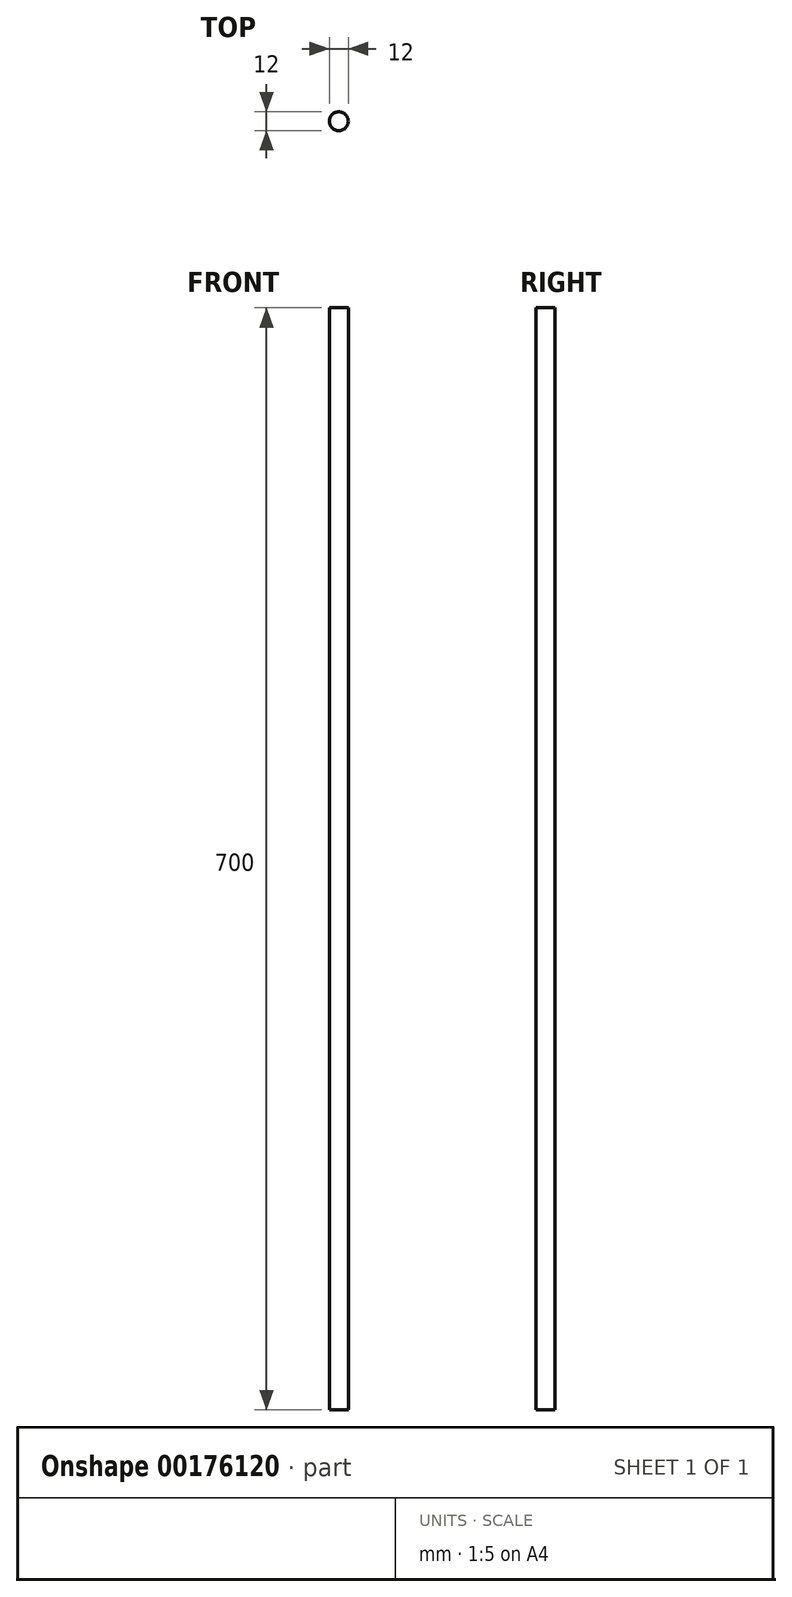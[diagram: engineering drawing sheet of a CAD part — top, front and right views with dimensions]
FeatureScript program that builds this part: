
annotation { "Feature Type Name" : "Feature", "Feature Type Description" : "" }
export const myFeature = defineFeature(function(context is Context, id is Id, definition is map)
    precondition{}
    {
        {
            var Q0;
            Q0=qCreatedBy(makeId("Top.planeOp"),FACE);
            var sketch = newSketch(context, id + "F0", { "sketchPlane" : qUnion([Q0])});
            skCircle(sketch, "E0", {"center": v(0, 0) * mm, "radius": 6 * mm});
            skSolve(sketch);
        }
        {
            var Q0;
            Q0 = qSketchRegion(id + "F0", true);
            extrude(context, id + "F1", {"entities" : qUnion([Q0]), "depth" : 700 * mm});
        }
    });
